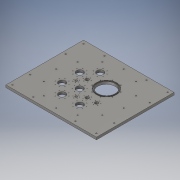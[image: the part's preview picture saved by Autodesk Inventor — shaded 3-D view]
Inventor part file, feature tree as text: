
AUTODESK INVENTOR PART (.ipt)
format: ipt  version: 2018 (Build 220112000, 112)  size: 591,872 bytes
history: native  units: in
note: dims shown in document units (in); Inventor stores cm internally (conversion verified against a paired STEP export)
features: sketch x28, hole x15, extrude x10, pattern_circular x6
ambient origin geometry x8: Origin, YZ Plane, XZ Plane, XY Plane, X Axis, Y Axis, Z Axis, Center Point
bodies: Solid1 (feature_tree)
feature tree (59):
  extrude  "Extrusion1"  Depth=24.0in
  sketch  "Sketch23"  dims[d16=0.252in d17=0.4in d18=0.375in d19=0.25in d20=0.5635in d21=0.5in d22=0.8108in d23=6.5in]
  extrude  "Extrusion2"  Depth=0.75in
  hole  "Hole1"  [1 undecoded]
  sketch  "Sketch58"  dims[d224=0.1in d225=0.0in]
  extrude  "Extrusion22"  Depth=1.0in TaperAngle=0.0deg
  extrude  "Extrusion29"  Depth=3.1496in TaperAngle=360.0deg
  extrude  "Extrusion3"  Depth=6.5in
  hole  "Hole2"  [1 undecoded]
  pattern_circular  "Circular Pattern1"  Count=8 Angle=360.0deg
  extrude  "Extrusion5"  Depth=3.5in
  hole  "Hole20"  [1 undecoded]
  extrude  "Extrusion16"  Depth=1.1811in TaperAngle=180.0deg
  hole  "Hole9"  [1 undecoded]
  pattern_circular  "Circular Pattern6"  Count=6 Angle=360.0deg
  extrude  "Extrusion18"  Depth=6.5in
  hole  "Hole10"  [1 undecoded]
  pattern_circular  "Circular Pattern7"  Count=8 Angle=360.0deg
  hole  "Hole13"  [1 undecoded]
  pattern_circular  "Circular Pattern9"  Count=12 Angle=360.0deg
  extrude  "Extrusion23"  Depth=0.75in
  hole  "Hole19"  [1 undecoded]
  pattern_circular  "Circular Pattern11"  [2 undecoded]
  extrude  "Extrusion27"  Depth=0.75in
  hole  "Hole23"  [1 undecoded]
  hole  "Hole18"  [1 undecoded]
  pattern_circular  "Circular Pattern12"  [2 undecoded]
  hole  "Hole22"  [1 undecoded]
  hole  "Hole24"  [1 undecoded]
  sketch  "Sketch57"  dims[d222=0.7902in d223=2.07in]
  sketch  "Sketch59"  dims[d229=1.625in d230=3.1496in d232=360.0deg]
  sketch  "Sketch62"  dims[d234=0.156in d235=0.38in d236=0.375in d237=0.25in d238=0.5635in d239=0.536in d240=0.8108in d242=0.7874in d243=90.0deg]
  hole  "Hole26"  [1 undecoded]
  hole  "Hole27"  [1 undecoded]
  hole  "Hole28"  [1 undecoded]
  hole  "Hole29"  [1 undecoded]
  sketch  "Sketch1"  dims[d0=28.0in d1=24.0in]
  sketch  "Sketch2"  dims[d2=0.75in d3=0.0in d4=3.6in]
  sketch  "Sketch3"  dims[d5=45.0deg d6=9.35in]
  sketch  "Sketch4"  dims[d7=5.4in d8=1.0in d9=0.0in]
  sketch  "Sketch7"  dims[d10=3.4in d12=3.1496in d14=360.0deg]
  sketch  "Sketch26"  dims[d24=1.4086in d25=2.07in]
  sketch  "Sketch28"  dims[d26=0.1in d27=0.0in]
  sketch  "Sketch30"  dims[d31=1.625in d33=3.1496in d35=360.0deg]
  sketch  "Sketch32"  dims[d37=0.156in d38=0.38in d39=0.375in d40=0.25in d41=0.5635in d42=0.536in d43=0.8108in d44=3.5in]
  sketch  "Sketch37"  dims[d45=2.0958in d46=1.04in]
  sketch  "Sketch38"  dims[d47=0.1in d48=0.0in d134=1.1811in d135=180.0deg]
  sketch  "Sketch39"  dims[d167=21.5in d168=19.125in]
  sketch  "Sketch45"  dims[d185=4.25in]
  sketch  "Sketch49"  dims[d186=180.0deg]
  sketch  "Sketch50"  dims[d187=0.68in]
  sketch  "Sketch51"  dims[d188=0.1in d189=0.0in]
  sketch  "Sketch53"  dims[d193=0.75in]
  sketch  "Sketch54"  dims[d194=180.0deg]
  sketch  "Sketch55"  dims[d195=0.156in d196=0.38in d197=0.375in d198=0.25in d199=0.5635in d200=0.536in d201=0.8108in d202=2.3622in d204=360.0deg]
  sketch  "Sketch56"  dims[d210=0.7874in d211=90.0deg d221=6.5in]
  sketch  "Sketch63"  dims[d277=10.4429in]
  sketch  "Sketch64"  dims[d278=0.354in d279=0.63in d280=0.375in d281=0.25in d282=0.5635in d283=0.831in d284=0.8108in d285=4.7244in d286=360.0deg]
  sketch  "Sketch65"  dims[d288=5.61in d289=5.93in d290=0.104in d291=0.0in d292=7.125in d293=15.125in d294=2.25in d295=135.0deg d296=2.07in d297=0.1in d298=0.0in d321=0.7874in d322=1.3743in d349=5.6in d350=30.0deg d351=1.04in d352=0.1in d353=0.0in d384=6.5in d385=0.0in d388=1.0in d389=45.0deg d390=1.5748in d392=360.0deg d394=0.171in d395=0.432in d396=0.375in d397=0.25in d398=0.5635in d399=0.64in d400=0.8108in d401=1.5748in d402=360.0deg d404=0.5in d405=22.5deg d406=0.5in d407=22.5deg d408=2.0in d409=22.5deg d410=1.625in d411=0.0in d412=3.1496in d414=360.0deg d416=0.156in d417=0.38in d418=0.375in d419=0.25in d420=0.5635in d421=0.536in d422=0.8108in d423=0.9449in d424=0.0in d425=2.3622in d427=360.0deg d429=0.156in d430=0.38in d431=0.375in d432=0.25in d433=0.5635in d434=0.536in d435=0.8108in d448=0.9449in d449=0.1512in d450=2.3622in d452=360.0deg d454=0.156in d455=0.38in d456=0.375in d457=0.25in d458=0.5635in d459=0.536in d460=0.8108in d461=0.9449in d462=30.0deg d463=2.3622in d465=360.0deg d467=0.156in d468=0.38in d469=0.375in d470=0.25in d471=0.5635in d472=0.536in d473=0.8108in d474=1.625in d475=22.5deg d476=3.1496in d478=360.0deg d480=0.156in d481=0.38in d482=0.375in d483=0.25in d484=0.5635in d485=0.536in d486=0.8108in d487=6.068in d488=6.35in d489=0.077in d490=0.0in d491=11.25in d492=14.5in d493=5.1in d494=3.7in d495=7.4in d498=11.0in d499=11.0in d500=10.0in d533=8.5in d534=0.2749in d535=8.5in d536=0.3436in d537=1.5748in d539=360.0deg d541=1.56in d542=45.0deg d543=4.706in d545=4.706in d546=180.0deg d547=0.196in d548=0.4in d549=0.375in d550=0.25in d551=0.5635in d552=0.6in d553=0.8108in d554=0.196in d555=0.4in d556=0.375in d557=0.25in d558=0.5635in d559=0.6in d560=0.8108in d561=1.56in d562=45.0deg d563=7.75in d564=0.8933in d565=7.75in d566=0.962in d567=0.196in d568=0.4in d569=0.375in d570=0.25in d571=0.5635in d572=0.6in d573=0.8108in d574=6.9473in d575=13.0in d576=0.7874in d578=360.0deg d580=26.0in d581=22.0in d582=6.5in d583=0.0in d584=0.397in d585=0.75in d586=0.762in d587=0.25in d588=0.5635in d589=1.0in d590=0.8108in d591=5.5in d592=5.5in]
note: 19 required parameter values undecoded (feature->parameter linkage not recoverable at this tier; creation-order binding heuristic only, values carry confidence <= 0.55)
